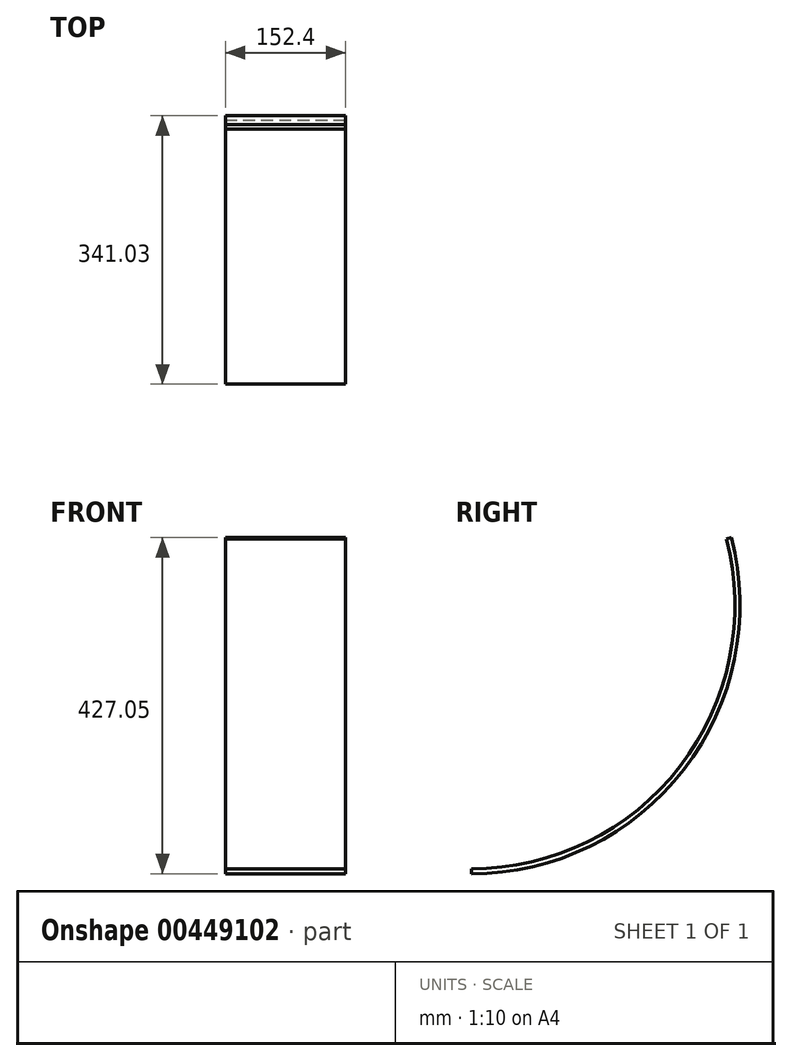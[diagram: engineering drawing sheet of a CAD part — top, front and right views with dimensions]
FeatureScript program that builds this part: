
annotation { "Feature Type Name" : "Feature", "Feature Type Description" : "" }
export const myFeature = defineFeature(function(context is Context, id is Id, definition is map)
    precondition{}
    {
        {
            var Q0;
            Q0=qCreatedBy(makeId("Right.planeOp"),FACE);
            var sketch = newSketch(context, id + "F0", { "sketchPlane" : qUnion([Q0])});
            skPoint(sketch, "E0.middle", {"position": v(-50.79, 18.9) * mm});
            skArc(sketch, "E1", {"start": v(-260.34, -190.64) * mm, "mid": v(4.49, -60.6) * mm, "end": v(63.52, 228.46) * mm});
            skPoint(sketch, "E2.orphan", {"position": v(-260.34, 228.46) * mm});
            skPoint(sketch, "E0.left.end.orphan", {"position": v(158.76, -190.64) * mm});
            skPoint(sketch, "E0.bottom.start.orphan", {"position": v(158.76, 228.46) * mm});
            skArc(sketch, "E3.0", {"start": v(-260.34, -197) * mm, "mid": v(9.51, -64.5) * mm, "end": v(69.67, 230.06) * mm});
            skLineSegment(sketch, "E4", {"start": v(-260.34, -190.64) * mm, "end": v(-260.34, -197) * mm});
            skLineSegment(sketch, "E5", {"start": v(63.52, 228.46) * mm, "end": v(69.67, 230.06) * mm});
            skSolve(sketch);
        }
        {
            var Q0;
            Q0 = qSketchRegion(id + "F0", true);
            extrude(context, id + "F1", {"entities" : qUnion([Q0]), "depth" : 152.4 * mm});
        }
    });
